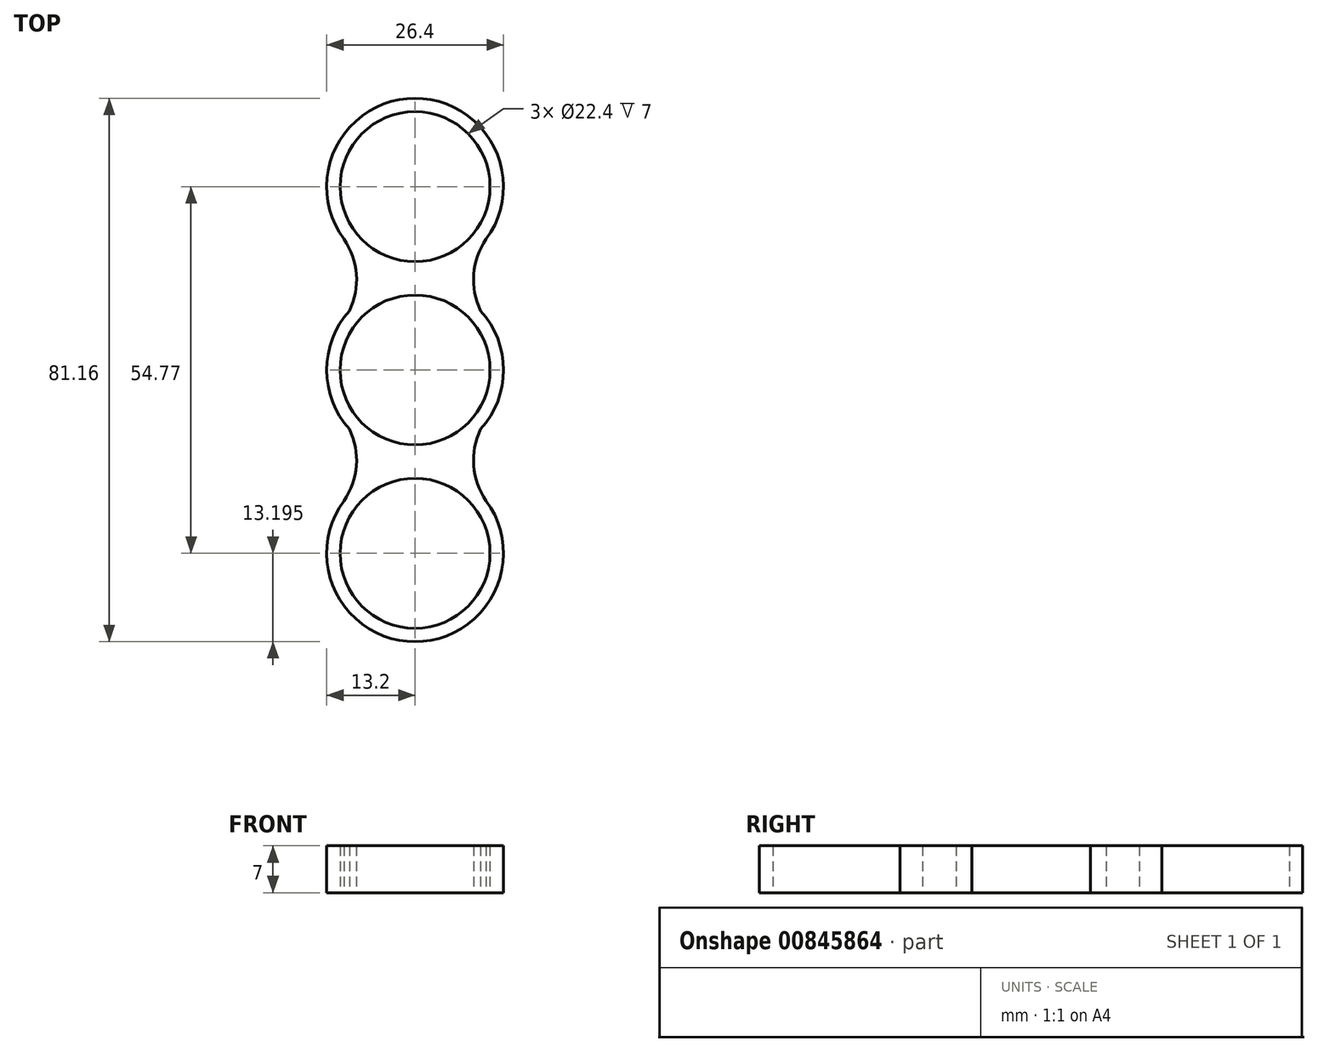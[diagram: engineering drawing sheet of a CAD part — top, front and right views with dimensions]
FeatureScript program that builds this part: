
annotation { "Feature Type Name" : "Feature", "Feature Type Description" : "" }
export const myFeature = defineFeature(function(context is Context, id is Id, definition is map)
    precondition{}
    {
        {
            var Q0;
            Q0=qCreatedBy(makeId("Top.planeOp"),FACE);
            var sketch = newSketch(context, id + "F0", { "sketchPlane" : qUnion([Q0])});
            skCircle(sketch, "E0", {"center": v(0, 0) * mm, "radius": 11.2 * mm});
            skCircle(sketch, "E1", {"center": v(0, 0) * mm, "radius": 13.2 * mm});
            skCircle(sketch, "E2", {"center": v(0, 27.38) * mm, "radius": 11.2 * mm});
            skCircle(sketch, "E3", {"center": v(0, 27.38) * mm, "radius": 13.2 * mm});
            skCircle(sketch, "E4.1.0", {"center": v(0, -27.38) * mm, "radius": 11.2 * mm});
            skCircle(sketch, "E4.1.1", {"center": v(0, -27.38) * mm, "radius": 13.2 * mm});
            skArc(sketch, "E5", {"start": v(-9.8, 8.85) * mm, "mid": v(-8.76, 14.3) * mm, "end": v(-10.61, 19.54) * mm});
            skArc(sketch, "E6.MirrorCS", {"start": v(9.8, 8.85) * mm, "mid": v(8.76, 14.3) * mm, "end": v(10.61, 19.54) * mm});
            skArc(sketch, "E7.MirrorCS", {"start": v(-9.8, -8.85) * mm, "mid": v(-8.76, -14.3) * mm, "end": v(-10.61, -19.54) * mm});
            skArc(sketch, "E8.MirrorCS", {"start": v(9.8, -8.85) * mm, "mid": v(8.76, -14.3) * mm, "end": v(10.61, -19.54) * mm});
            skSolve(sketch);
        }
        {
            var Q0;
            Q0 = qSketchRegion(id + "F0", true);
            extrude(context, id + "F1", {"entities" : qUnion([Q0]), "depth" : 7 * mm, "offsetDistance" : 25 * mm});
        }
    });
